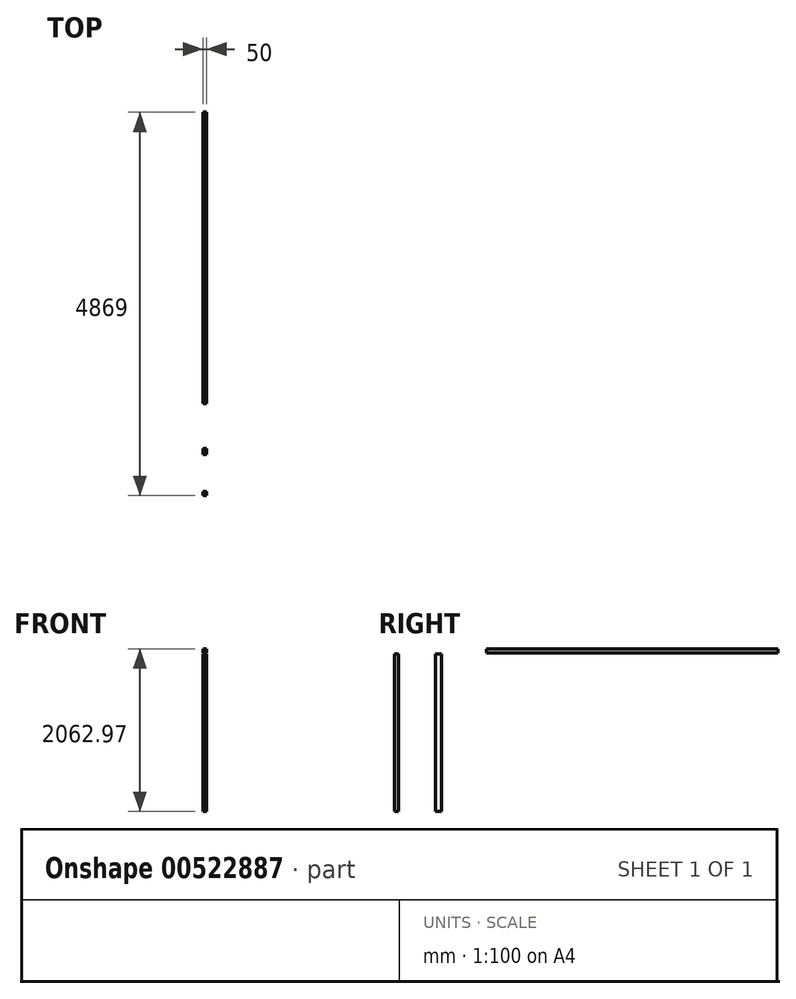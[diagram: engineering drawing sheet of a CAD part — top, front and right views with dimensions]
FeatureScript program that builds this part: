
annotation { "Feature Type Name" : "Feature", "Feature Type Description" : "" }
export const myFeature = defineFeature(function(context is Context, id is Id, definition is map)
    precondition{}
    {
        {
            var Q0;
            Q0=qCreatedBy(makeId("Right.planeOp"),FACE);
            var sketch = newSketch(context, id + "F0", { "sketchPlane" : qUnion([Q0])});
            skLineSegment(sketch, "E0", {"start": v(-397.99, 41.64) * mm, "end": v(3302.01, 41.64) * mm});
            skLineSegment(sketch, "E1", {"start": v(3302.01, 41.64) * mm, "end": v(3302.01, -8.36) * mm});
            skLineSegment(sketch, "E2", {"start": v(3302.01, -8.36) * mm, "end": v(-397.99, -8.36) * mm});
            skLineSegment(sketch, "E3", {"start": v(-397.99, -8.36) * mm, "end": v(-397.99, 41.64) * mm});
            skLineSegment(sketch, "E4", {"start": v(-1046.34, -21.33) * mm, "end": v(-971.34, -21.33) * mm});
            skLineSegment(sketch, "E5", {"start": v(-971.34, -21.33) * mm, "end": v(-971.34, -2021.33) * mm});
            skLineSegment(sketch, "E6", {"start": v(-971.34, -2021.33) * mm, "end": v(-1046.34, -2021.33) * mm});
            skLineSegment(sketch, "E7", {"start": v(-1046.34, -2021.33) * mm, "end": v(-1046.34, -21.33) * mm});
            skLineSegment(sketch, "E8", {"start": v(-1566.99, -21.33) * mm, "end": v(-1516.99, -21.33) * mm});
            skLineSegment(sketch, "E9", {"start": v(-1516.99, -21.33) * mm, "end": v(-1516.99, -2021.33) * mm});
            skLineSegment(sketch, "E10", {"start": v(-1516.99, -2021.33) * mm, "end": v(-1566.99, -2021.33) * mm});
            skLineSegment(sketch, "E11", {"start": v(-1566.99, -2021.33) * mm, "end": v(-1566.99, -21.33) * mm});
            skSolve(sketch);
        }
        {
            var Q0;
            Q0=makeQuery(id+"F0.imprint","IMPRINT",FACE,{"disambiguationData":[TD([[makeQuery(id+"F0.imprint","IMPRINT",EDGE,{"derivedFrom":sQuery(id+"F0.wireOp",EDGE,"E0")}),-1.0]])]});
            var Q1;
            Q1=makeQuery(id+"F0.imprint","IMPRINT",FACE,{"disambiguationData":[TD([[makeQuery(id+"F0.imprint","IMPRINT",EDGE,{"derivedFrom":sQuery(id+"F0.wireOp",EDGE,"E4")}),-1.0]])]});
            var Q2;
            Q2=makeQuery(id+"F0.imprint","IMPRINT",FACE,{"disambiguationData":[TD([[makeQuery(id+"F0.imprint","IMPRINT",EDGE,{"derivedFrom":sQuery(id+"F0.wireOp",EDGE,"E8")}),-1.0]])]});
            extrude(context, id + "F1", {"entities" : qUnion([Q0, Q1, Q2]), "depth" : 50 * mm, "offsetDistance" : 25 * mm});
        }
    });
